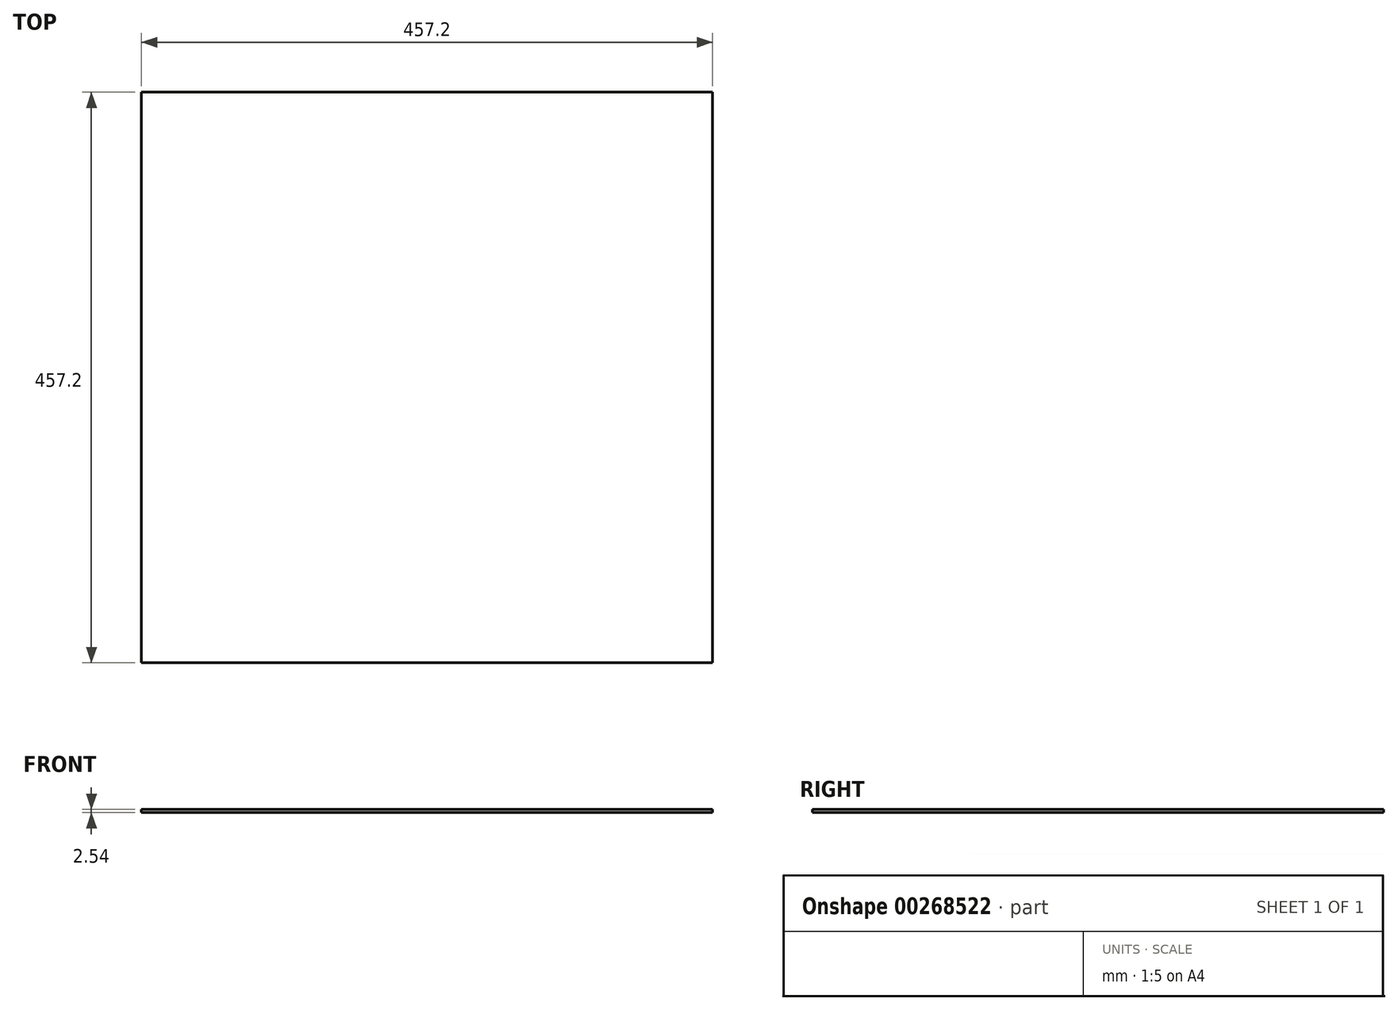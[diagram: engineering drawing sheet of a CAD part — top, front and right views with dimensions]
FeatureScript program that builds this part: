
annotation { "Feature Type Name" : "Feature", "Feature Type Description" : "" }
export const myFeature = defineFeature(function(context is Context, id is Id, definition is map)
    precondition{}
    {
        {
            var Q0;
            Q0=qCreatedBy(makeId("Top.planeOp"),FACE);
            var sketch = newSketch(context, id + "F0", { "sketchPlane" : qUnion([Q0])});
            skLineSegment(sketch, "E0.bottom", {"start": v(0, 0) * mm, "end": v(457.2, 0) * mm});
            skLineSegment(sketch, "E0.top", {"start": v(0, -457.2) * mm, "end": v(457.2, -457.2) * mm});
            skLineSegment(sketch, "E0.left", {"start": v(0, 0) * mm, "end": v(0, -457.2) * mm});
            skLineSegment(sketch, "E0.right", {"start": v(457.2, 0) * mm, "end": v(457.2, -457.2) * mm});
            skSolve(sketch);
        }
        {
            var Q0;
            Q0 = qSketchRegion(id + "F0", true);
            extrude(context, id + "F1", {"entities" : qUnion([Q0]), "depth" : 2.54 * mm});
        }
    });
